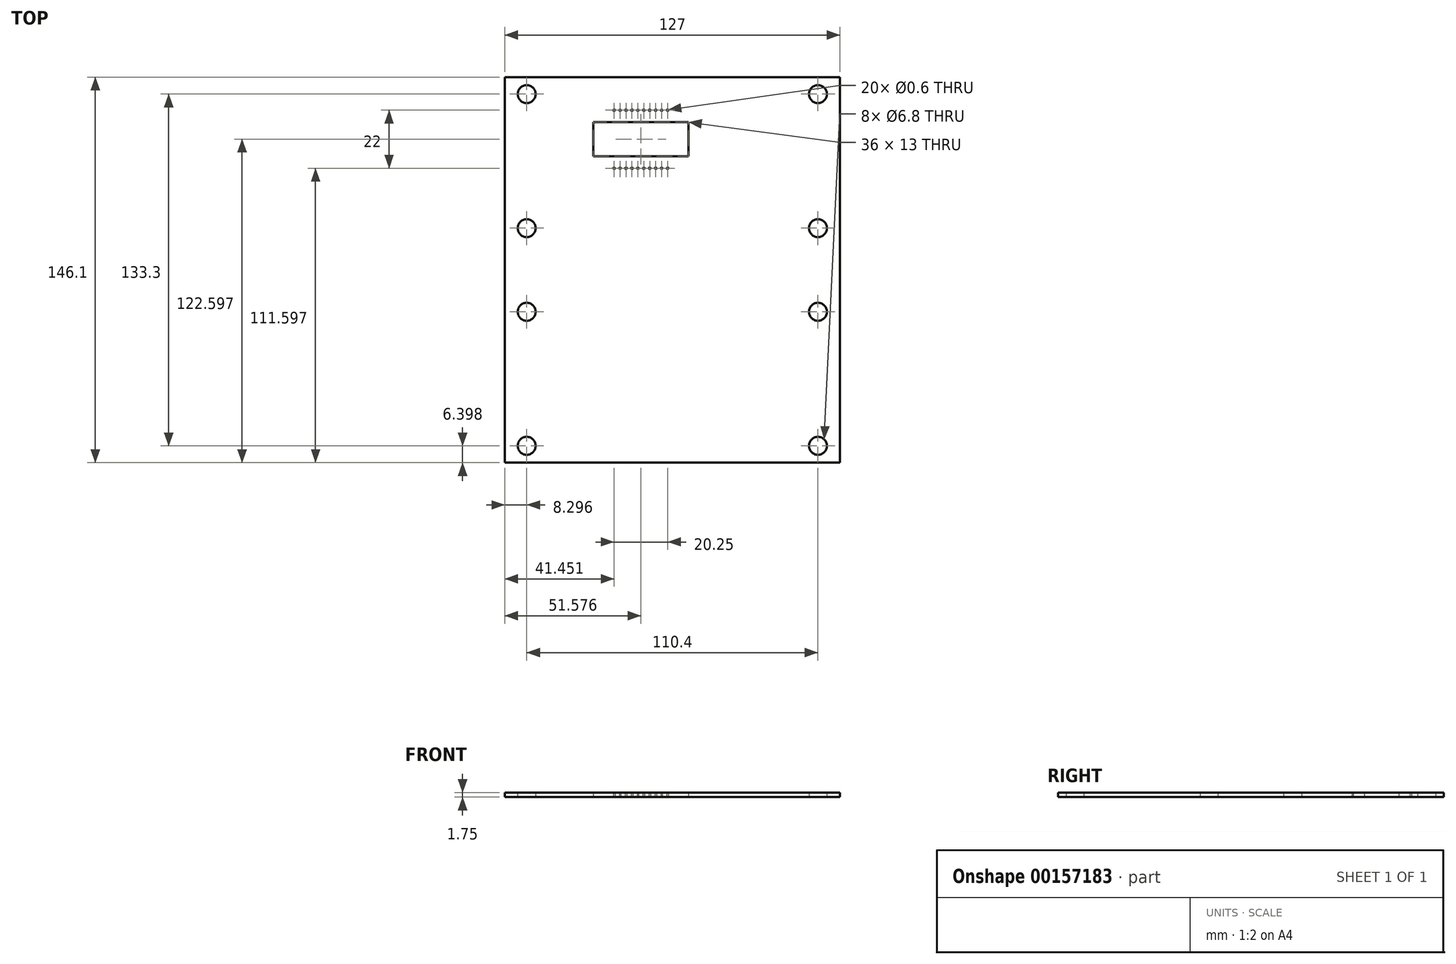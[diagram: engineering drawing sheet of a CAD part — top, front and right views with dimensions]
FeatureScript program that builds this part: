
annotation { "Feature Type Name" : "Feature", "Feature Type Description" : "" }
export const myFeature = defineFeature(function(context is Context, id is Id, definition is map)
    precondition{}
    {
        {
            var Q0;
            Q0=qCreatedBy(makeId("Top.planeOp"),FACE);
            var sketch = newSketch(context, id + "F0", { "sketchPlane" : qUnion([Q0])});
            skLineSegment(sketch, "E0.bottom", {"start": v(-68.08, 83.86) * mm, "end": v(58.92, 83.86) * mm});
            skLineSegment(sketch, "E0.top", {"start": v(-68.08, -62.24) * mm, "end": v(58.92, -62.24) * mm});
            skLineSegment(sketch, "E0.left", {"start": v(-68.08, 83.86) * mm, "end": v(-68.08, -62.24) * mm});
            skLineSegment(sketch, "E0.right", {"start": v(58.92, 83.86) * mm, "end": v(58.92, -62.24) * mm});
            skLineSegment(sketch, "E1", {"start": v(-59.78, 83.86) * mm, "end": v(-59.78, -62.24) * mm, "construction": true});
            skLineSegment(sketch, "E2", {"start": v(50.62, 83.86) * mm, "end": v(50.62, -62.24) * mm, "construction": true});
            skCircle(sketch, "E3", {"center": v(-59.78, 77.46) * mm, "radius": 3.4 * mm});
            skCircle(sketch, "E4", {"center": v(-59.78, 26.66) * mm, "radius": 3.4 * mm});
            skCircle(sketch, "E5", {"center": v(-59.78, -5.04) * mm, "radius": 3.4 * mm});
            skCircle(sketch, "E6", {"center": v(-59.78, -55.84) * mm, "radius": 3.4 * mm});
            skCircle(sketch, "E7", {"center": v(50.62, -55.84) * mm, "radius": 3.4 * mm});
            skCircle(sketch, "E8", {"center": v(50.62, -5.04) * mm, "radius": 3.4 * mm});
            skCircle(sketch, "E9", {"center": v(50.62, 26.66) * mm, "radius": 3.4 * mm});
            skCircle(sketch, "E10", {"center": v(50.62, 77.46) * mm, "radius": 3.4 * mm});
            skLineSegment(sketch, "E11", {"start": v(-29.44, 71.36) * mm, "end": v(24.83, 71.36) * mm, "construction": true});
            skCircle(sketch, "E12", {"center": v(-26.63, 71.36) * mm, "radius": 0.3 * mm});
            skLineSegment(sketch, "E13", {"start": v(-32.94, 49.36) * mm, "end": v(16.35, 49.36) * mm, "construction": true});
            skCircle(sketch, "E14.1.0.0", {"center": v(-24.38, 71.36) * mm, "radius": 0.3 * mm});
            skCircle(sketch, "E14.2.0.0", {"center": v(-22.13, 71.36) * mm, "radius": 0.3 * mm});
            skCircle(sketch, "E14.3.0.0", {"center": v(-19.88, 71.36) * mm, "radius": 0.3 * mm});
            skCircle(sketch, "E14.4.0.0", {"center": v(-17.63, 71.36) * mm, "radius": 0.3 * mm});
            skCircle(sketch, "E14.5.0.0", {"center": v(-15.38, 71.36) * mm, "radius": 0.3 * mm});
            skCircle(sketch, "E14.6.0.0", {"center": v(-13.13, 71.36) * mm, "radius": 0.3 * mm});
            skCircle(sketch, "E14.7.0.0", {"center": v(-10.88, 71.36) * mm, "radius": 0.3 * mm});
            skCircle(sketch, "E14.8.0.0", {"center": v(-8.63, 71.36) * mm, "radius": 0.3 * mm});
            skCircle(sketch, "E14.9.0.0", {"center": v(-6.38, 71.36) * mm, "radius": 0.3 * mm});
            skLineSegment(sketch, "E14.direction1", {"start": v(-26.63, 71.36) * mm, "end": v(-24.38, 71.36) * mm, "construction": true});
            skCircle(sketch, "E15", {"center": v(-26.63, 49.36) * mm, "radius": 0.3 * mm});
            skCircle(sketch, "E16.1.0.0", {"center": v(-24.38, 49.36) * mm, "radius": 0.3 * mm});
            skCircle(sketch, "E16.2.0.0", {"center": v(-22.13, 49.36) * mm, "radius": 0.3 * mm});
            skCircle(sketch, "E16.3.0.0", {"center": v(-19.88, 49.36) * mm, "radius": 0.3 * mm});
            skCircle(sketch, "E16.4.0.0", {"center": v(-17.63, 49.36) * mm, "radius": 0.3 * mm});
            skCircle(sketch, "E16.5.0.0", {"center": v(-15.38, 49.36) * mm, "radius": 0.3 * mm});
            skCircle(sketch, "E16.6.0.0", {"center": v(-13.13, 49.36) * mm, "radius": 0.3 * mm});
            skCircle(sketch, "E16.7.0.0", {"center": v(-10.88, 49.36) * mm, "radius": 0.3 * mm});
            skCircle(sketch, "E16.8.0.0", {"center": v(-8.63, 49.36) * mm, "radius": 0.3 * mm});
            skCircle(sketch, "E16.9.0.0", {"center": v(-6.38, 49.36) * mm, "radius": 0.3 * mm});
            skLineSegment(sketch, "E16.direction1", {"start": v(-26.63, 49.36) * mm, "end": v(-24.38, 49.36) * mm, "construction": true});
            skLineSegment(sketch, "E17.bottom", {"start": v(-34.5, 66.86) * mm, "end": v(1.5, 66.86) * mm});
            skLineSegment(sketch, "E17.top", {"start": v(-34.5, 53.86) * mm, "end": v(1.5, 53.86) * mm});
            skLineSegment(sketch, "E17.left", {"start": v(-34.5, 66.86) * mm, "end": v(-34.5, 53.86) * mm});
            skLineSegment(sketch, "E17.right", {"start": v(1.5, 66.86) * mm, "end": v(1.5, 53.86) * mm});
            skSolve(sketch);
        }
        {
            var Q0;
            Q0 = qSketchRegion(id + "F0", true);
            extrude(context, id + "F1", {"entities" : qUnion([Q0]), "depth" : 1.75 * mm});
        }
    });
